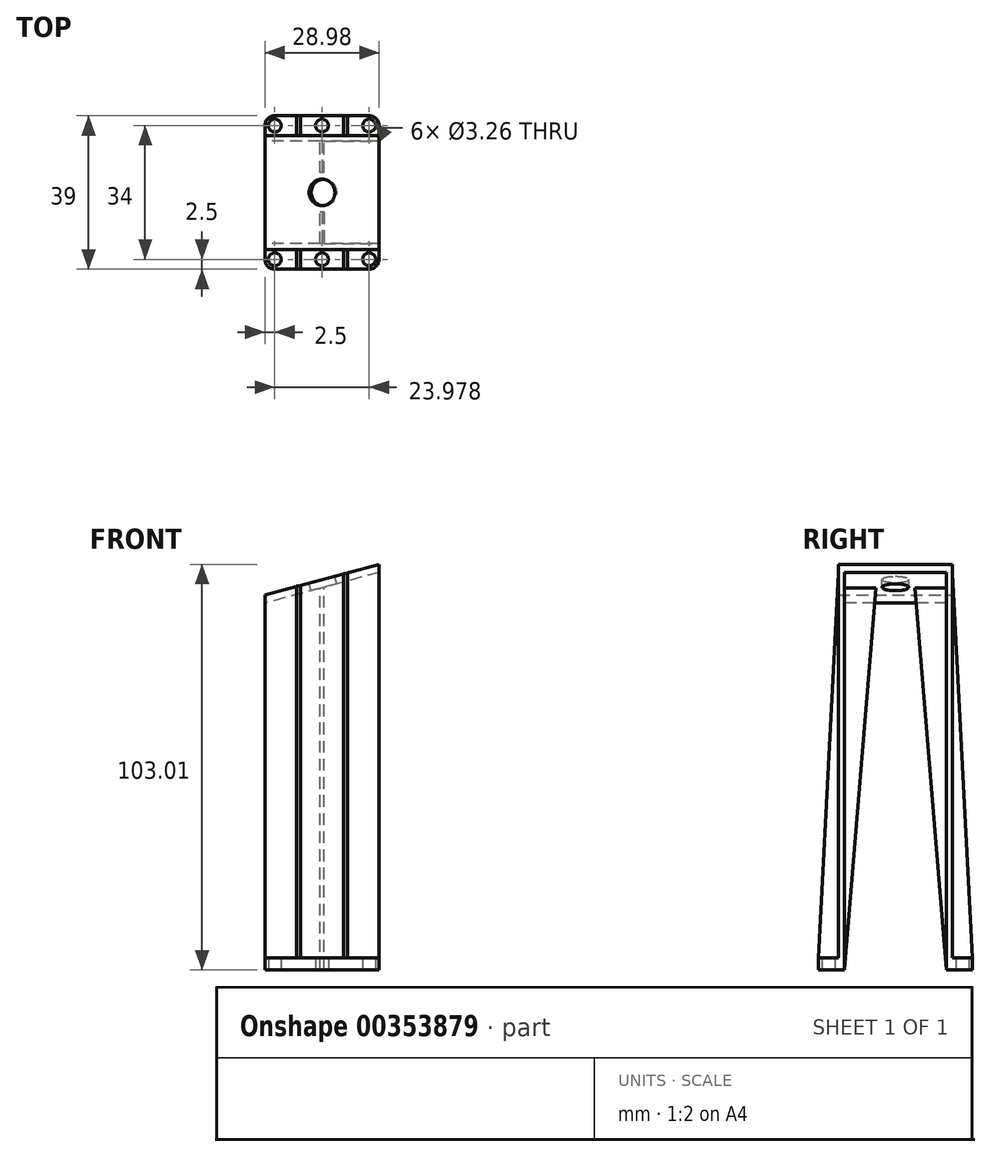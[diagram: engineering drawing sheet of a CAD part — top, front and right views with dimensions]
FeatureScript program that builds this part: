
annotation { "Feature Type Name" : "Feature", "Feature Type Description" : "" }
export const myFeature = defineFeature(function(context is Context, id is Id, definition is map)
    precondition{}
    {
        {
            var Q0;
            Q0=qCreatedBy(makeId("Front.planeOp"),FACE);
            var sketch = newSketch(context, id + "F0", { "sketchPlane" : qUnion([Q0])});
            skLineSegment(sketch, "E0", {"start": v(0, 0) * mm, "end": v(28.98, 7.76) * mm});
            skLineSegment(sketch, "E1", {"start": v(28.98, 7.76) * mm, "end": v(28.98, 0) * mm});
            skLineSegment(sketch, "E2", {"start": v(28.98, 0) * mm, "end": v(0, 0) * mm});
            skLineSegment(sketch, "E3.top", {"start": v(28.98, -95.25) * mm, "end": v(0, -95.25) * mm});
            skLineSegment(sketch, "E3.left", {"start": v(28.98, 0) * mm, "end": v(28.98, -95.25) * mm});
            skLineSegment(sketch, "E3.right", {"start": v(0, 0) * mm, "end": v(0, -95.25) * mm});
            skSolve(sketch);
        }
        {
            var Q0;
            Q0=makeQuery(id+"F0.imprint","IMPRINT",FACE,{"disambiguationData":[TD([[makeQuery(id+"F0.imprint","IMPRINT",EDGE,{"derivedFrom":sQuery(id+"F0.wireOp",EDGE,"E0")}),-1.0]])]});
            var Q1;
            Q1=sQuery(id+"F0.wireOp",EDGE,"E0");
            var Q2;
            Q2=sQuery(id+"F0.wireOp",EDGE,"E1");
            var Q3;
            Q3=sQuery(id+"F0.wireOp",EDGE,"E3.left");
            var Q4;
            Q4=sQuery(id+"F0.wireOp",EDGE,"E3.top");
            var Q5;
            Q5=sQuery(id+"F0.wireOp",EDGE,"E3.right");
            extrude(context, id + "F1", {"entities" : qUnion([Q0]), "surfaceEntities" : qUnion([Q1, Q2, Q3, Q4, Q5]), "depth" : 29 * mm});
        }
        {
            var Q0;
            Q0 = qSketchRegion(id + "F0", true);
            extrude(context, id + "F2", {"entities" : qUnion([Q0]), "operationType" : NewBodyOperationType.ADD, "depth" : 29 * mm});
        }
        {
            var Q0;
            Q0=makeQuery(id+"F1.opExtrude","SWEPT_FACE",FACE,{"disambiguationData":[OSD([sQuery(id+"F0.wireOp",EDGE,"E0")])]});
            var sketch = newSketch(context, id + "F3", { "sketchPlane" : qUnion([Q0])});
            skPoint(sketch, "E4", {"position": v(0, -14.5) * mm});
            skPoint(sketch, "E5", {"position": v(15, 0) * mm});
            skLineSegment(sketch, "E6", {"start": v(0, -14.5) * mm, "end": v(30, -14.5) * mm});
            skLineSegment(sketch, "E7", {"start": v(15, 0) * mm, "end": v(15, -29) * mm});
            skPoint(sketch, "E8", {"position": v(15, -20.5) * mm});
            skPoint(sketch, "E9", {"position": v(26, -14.5) * mm});
            skLineSegment(sketch, "E10.bottom", {"start": v(15, -20.5) * mm, "end": v(26, -20.5) * mm});
            skLineSegment(sketch, "E10.top", {"start": v(15, -14.5) * mm, "end": v(26, -14.5) * mm});
            skLineSegment(sketch, "E10.left", {"start": v(15, -20.5) * mm, "end": v(15, -14.5) * mm});
            skLineSegment(sketch, "E10.right", {"start": v(26, -20.5) * mm, "end": v(26, -14.5) * mm});
            skPoint(sketch, "E11", {"position": v(26, -20.5) * mm});
            skCircle(sketch, "E12", {"center": v(26, -20.5) * mm, "radius": 1.2 * mm});
            skCircle(sketch, "E13.MirrorC", {"center": v(4, -20.5) * mm, "radius": 1.2 * mm});
            skCircle(sketch, "E14.MirrorC", {"center": v(4, -8.5) * mm, "radius": 1.2 * mm});
            skCircle(sketch, "E15.MirrorC", {"center": v(26, -8.5) * mm, "radius": 1.2 * mm});
            skSolve(sketch);
        }
        {
            var Q0;
            Q0=makeQuery(id+"F2.opExtrude","SWEPT_FACE",FACE,{"disambiguationData":[OSD([sQuery(id+"F0.wireOp",EDGE,"E3.top")])]});
            var sketch = newSketch(context, id + "F4", { "sketchPlane" : qUnion([Q0])});
            skPoint(sketch, "E16", {"position": v(2.5, 31.5) * mm});
            skLineSegment(sketch, "E17", {"start": v(14.49, 29) * mm, "end": v(14.49, 0) * mm});
            skPoint(sketch, "E18.MirrorP", {"position": v(26.48, 31.5) * mm});
            skPoint(sketch, "E19", {"position": v(14.49, 31.5) * mm});
            skLineSegment(sketch, "E20.bottom", {"start": v(28.98, 29) * mm, "end": v(0, 29) * mm});
            skLineSegment(sketch, "E20.top", {"start": v(28.98, 34) * mm, "end": v(0, 34) * mm});
            skLineSegment(sketch, "E20.left", {"start": v(28.98, 29) * mm, "end": v(28.98, 34) * mm});
            skLineSegment(sketch, "E20.right", {"start": v(0, 29) * mm, "end": v(0, 34) * mm});
            skLineSegment(sketch, "E21", {"start": v(0, 14.5) * mm, "end": v(28.98, 14.5) * mm});
            skLineSegment(sketch, "E22.MirrorCS", {"start": v(28.98, 0) * mm, "end": v(0, 0) * mm});
            skLineSegment(sketch, "E23.MirrorCS", {"start": v(0, 0) * mm, "end": v(0, -5) * mm});
            skLineSegment(sketch, "E24.MirrorCS", {"start": v(28.98, -5) * mm, "end": v(0, -5) * mm});
            skLineSegment(sketch, "E25.MirrorCS", {"start": v(28.98, 0) * mm, "end": v(28.98, -5) * mm});
            skPoint(sketch, "E26.MirrorP", {"position": v(26.48, -2.5) * mm});
            skPoint(sketch, "E27.MirrorP", {"position": v(14.49, -2.5) * mm});
            skPoint(sketch, "E28.MirrorP", {"position": v(2.5, -2.5) * mm});
            skSolve(sketch);
        }
        {
            var Q0;
            Q0=makeQuery(id+"F4.imprint","IMPRINT",FACE,{"disambiguationData":[TD([[makeQuery(id+"F4.imprint","IMPRINT",EDGE,{"derivedFrom":sQuery(id+"F4.wireOp",EDGE,"E20.top")}),1.0]])]});
            var Q1;
            {var subQ4=sQuery(id+"F4.wireOp",EDGE,"c207b0aa-8032-4c64-916d-486b236da78c0.MirrorCS");Q1=makeQuery(id+"F4.imprint","IMPRINT",FACE,{"disambiguationData":[TD([[makeQuery(id+"F4.imprint","IMPRINT",EDGE,{"derivedFrom":subQ4}),1.0]])]});}
            var Q2;
            {var subQ0=sQuery(id+"F4.wireOp",EDGE,"E23.MirrorCS");Q2=makeQuery(id+"F4.imprint","IMPRINT",FACE,{"disambiguationData":[TD([[makeQuery(id+"F4.imprint","IMPRINT",EDGE,{"derivedFrom":subQ0}),1.0]])]});}
            extrude(context, id + "F5", {"entities" : qUnion([Q0, Q1, Q2]), "operationType" : NewBodyOperationType.ADD, "oppositeDirection" : true, "depth" : 3 * mm});
        }
        {
            var Q0;
            Q0=makeQuery(id+"F5.opExtrude","SWEPT_EDGE",EDGE,{"disambiguationData":[OSD([sQuery(id+"F4.wireOp",EDGE,"E20.top"),sQuery(id+"F4.wireOp",EDGE,"E20.left")])]});
            var Q1;
            Q1=makeQuery(id+"F5.opExtrude","SWEPT_EDGE",EDGE,{"disambiguationData":[OSD([sQuery(id+"F4.wireOp",EDGE,"E20.top"),sQuery(id+"F4.wireOp",EDGE,"E20.right")])]});
            var Q2;
            Q2=makeQuery(id+"F5.opExtrude","SWEPT_EDGE",EDGE,{"disambiguationData":[OSD([sQuery(id+"F4.wireOp",EDGE,"fb5fafe6-6dba-495f-bc75-69146ea7bf050.MirrorCS"),sQuery(id+"F4.wireOp",EDGE,"04278182-d480-4ec0-bce9-3d76de338e120.MirrorCS")])]});
            var Q3;
            Q3=makeQuery(id+"F5.opExtrude","SWEPT_EDGE",EDGE,{"disambiguationData":[OSD([sQuery(id+"F4.wireOp",EDGE,"c207b0aa-8032-4c64-916d-486b236da78c0.MirrorCS"),sQuery(id+"F4.wireOp",EDGE,"fb5fafe6-6dba-495f-bc75-69146ea7bf050.MirrorCS")])]});
            fillet(context, id + "F6", {"entities" : qUnion([Q0, Q1, Q2, Q3]), "radius" : 2.5 * mm, "tangentPropagation" : true, "allowEdgeOverflow" : false});
        }
        {
            var Q0;
            Q0=sQuery(id+"F4.wireOp",VERTEX,"1afc1c53-2bd5-44ff-b609-8fd2801f01ae0.MirrorP");
            var Q1;
            Q1=sQuery(id+"F4.wireOp",VERTEX,"2608caf0-84c1-456a-a7c5-d9c789f694d10.MirrorP");
            var Q2;
            Q2=sQuery(id+"F4.wireOp",VERTEX,"cd476bde-2b93-4753-bf9c-91846a678cbf0.MirrorP");
            var Q3;
            Q3=sQuery(id+"F4.wireOp",VERTEX,"E16");
            var Q4;
            Q4=sQuery(id+"F4.wireOp",VERTEX,"E19");
            var Q5;
            Q5=sQuery(id+"F4.wireOp",VERTEX,"E18.MirrorP");
            var Q6;
            Q6=sQuery(id+"F4.wireOp",VERTEX,"E28.MirrorP");
            var Q7;
            Q7=sQuery(id+"F4.wireOp",VERTEX,"E27.MirrorP");
            var Q8;
            Q8=sQuery(id+"F4.wireOp",VERTEX,"E26.MirrorP");
            var Q9;
            Q9=makeQuery(id+"F1.opExtrude","SWEPT_BODY",BODY,{"disambiguationData":[OSD([sQuery(id+"F0.wireOp",EDGE,"E0"),sQuery(id+"F0.wireOp",EDGE,"E1"),sQuery(id+"F0.wireOp",EDGE,"E2")])]});
            hole(context, id + "F7", {"style" : HoleStyle.SIMPLE, "endStyle" : HoleEndStyle.THROUGH, "holeDiameter" : 3.26 * mm, "isTappedThrough" : true, "tappedDepth" : 12.7 * mm, "tapClearance" : 3, "locations" : qUnion([Q0, Q1, Q2, Q3, Q4, Q5, Q6, Q7, Q8]), "scope" : qUnion([Q9])});
        }
        {
            var Q0;
            Q0=makeQuery(id+"F1.opExtrude","SWEPT_FACE",FACE,{"disambiguationData":[OSD([sQuery(id+"F0.wireOp",EDGE,"E0")])]});
            cPlane(context, id + "F8", {"entities" : qUnion([Q0]), "cplaneType" : CPlaneType.OFFSET, "offset" : 2 * mm, "oppositeDirection" : true, "width" : 152.4 * mm, "height" : 152.4 * mm});
        }
        {
            var Q0;
            Q0=qCreatedBy(id+"F8.planeOp",FACE);
            var sketch = newSketch(context, id + "F9", { "sketchPlane" : qUnion([Q0])});
            skLineSegment(sketch, "E29", {"start": v(-0.54, -29) * mm, "end": v(29.46, -29) * mm});
            skLineSegment(sketch, "E30", {"start": v(-0.54, 0) * mm, "end": v(29.46, 0) * mm});
            skLineSegment(sketch, "E31", {"start": v(29.46, -29) * mm, "end": v(29.46, 0) * mm});
            skLineSegment(sketch, "E32.bottom", {"start": v(29.46, -27.5) * mm, "end": v(-30.54, -27.5) * mm});
            skLineSegment(sketch, "E32.top", {"start": v(29.46, -1.5) * mm, "end": v(-30.54, -1.5) * mm});
            skLineSegment(sketch, "E32.left", {"start": v(29.46, -27.5) * mm, "end": v(29.46, -1.5) * mm});
            skLineSegment(sketch, "E32.right", {"start": v(-30.54, -27.5) * mm, "end": v(-30.54, -1.5) * mm});
            skPoint(sketch, "E32.middle", {"position": v(-0.54, -14.5) * mm});
            skSolve(sketch);
        }
        {
            var Q0;
            Q0=makeQuery(id+"F5.opExtrude","SWEPT_EDGE",EDGE,{"disambiguationData":[OSD([sQuery(id+"F4.wireOp",EDGE,"E24.MirrorCS"),sQuery(id+"F4.wireOp",EDGE,"E25.MirrorCS")])]});
            var Q1;
            Q1=makeQuery(id+"F5.opExtrude","SWEPT_EDGE",EDGE,{"disambiguationData":[OSD([sQuery(id+"F4.wireOp",EDGE,"E23.MirrorCS"),sQuery(id+"F4.wireOp",EDGE,"E24.MirrorCS")])]});
            fillet(context, id + "F10", {"entities" : qUnion([Q0, Q1]), "radius" : 2.5 * mm, "tangentPropagation" : true, "allowEdgeOverflow" : false});
        }
        {
            var Q0;
            Q0=makeQuery(id+"F9.imprint","IMPRINT",FACE,{"disambiguationData":[TD([[makeQuery(id+"F9.imprint","IMPRINT",EDGE,{"derivedFrom":sQuery(id+"F9.wireOp",EDGE,"E32.bottom")}),-1.0]])]});
            var Q1;
            Q1=sQuery(id+"F9.wireOp",EDGE,"E32.bottom");
            var Q2;
            Q2=sQuery(id+"F9.wireOp",EDGE,"E32.right");
            var Q3;
            Q3=sQuery(id+"F9.wireOp",EDGE,"E32.top");
            var Q4;
            Q4=sQuery(id+"F9.wireOp",EDGE,"E32.left");
            extrude(context, id + "F11", {"entities" : qUnion([Q0]), "operationType" : NewBodyOperationType.REMOVE, "surfaceEntities" : qUnion([Q1, Q2, Q3, Q4]), "endBound" : BoundingType.THROUGH_ALL, "oppositeDirection" : true, "depth" : 25 * mm});
        }
        {
            var Q0;
            Q0=makeQuery(id+"F5.opExtrude","CAP_FACE",FACE,{"disambiguationData":[OSD([sQuery(id+"F4.wireOp",EDGE,"E20.bottom"),sQuery(id+"F4.wireOp",EDGE,"E20.top"),sQuery(id+"F4.wireOp",EDGE,"E20.left"),sQuery(id+"F4.wireOp",EDGE,"E20.right")])],"isStart":false});
            var sketch = newSketch(context, id + "F12", { "sketchPlane" : qUnion([Q0])});
            skLineSegment(sketch, "E33", {"start": v(2.5, -31.5) * mm, "end": v(14.49, -31.5) * mm});
            skLineSegment(sketch, "E34", {"start": v(26.48, -31.5) * mm, "end": v(14.49, -31.5) * mm});
            skPoint(sketch, "E35", {"position": v(8.5, -31.5) * mm});
            skPoint(sketch, "E36", {"position": v(20.48, -31.5) * mm});
            skSolve(sketch);
        }
        {
            var Q0;
            Q0=sQuery(id+"F12.wireOp",EDGE,"E34");
            cPoint(context, id + "F13", {"entities" : qUnion([Q0]), "parameter" : 0.5});
        }
        {
            var Q0;
            {var subQ0=sQuery(id+"F0.wireOp",EDGE,"E1");Q0=makeQuery(id+"F5.boolean.opBoolean","MERGE",FACE,{"derivedFrom":[makeQuery(id+"F2.boolean.opBoolean","MERGE",FACE,{"derivedFrom":[makeQuery(id+"F1.opExtrude","SWEPT_FACE",FACE,{"disambiguationData":[OSD([subQ0])]}),makeQuery(id+"F2.opExtrude","SWEPT_FACE",FACE,{"disambiguationData":[OSD([subQ0,sQuery(id+"F0.wireOp",EDGE,"E3.left")])]})]}),makeQuery(id+"F5.opExtrude","SWEPT_FACE",FACE,{"disambiguationData":[OSD([sQuery(id+"F4.wireOp",EDGE,"E20.left")])]}),makeQuery(id+"F5.opExtrude","SWEPT_FACE",FACE,{"disambiguationData":[OSD([sQuery(id+"F4.wireOp",EDGE,"E25.MirrorCS")])]})]});}
            var Q1;
            Q1 = qCreatedBy(id + "F13" ,VERTEX);
            cPlane(context, id + "F14", {"entities" : qUnion([Q0, Q1]), "cplaneType" : CPlaneType.PLANE_POINT, "offset" : 25 * mm, "width" : 150 * mm, "height" : 150 * mm});
        }
        {
            var Q0;
            Q0=qCreatedBy(id+"F14.planeOp",FACE);
            var sketch = newSketch(context, id + "F15", { "sketchPlane" : qUnion([Q0])});
            skLineSegment(sketch, "E37", {"start": v(-29, 5.49) * mm, "end": v(-29, -92.25) * mm});
            skLineSegment(sketch, "E38", {"start": v(-29, -92.25) * mm, "end": v(-34, -92.25) * mm});
            skLineSegment(sketch, "E39", {"start": v(-29, 5.49) * mm, "end": v(-34, -92.25) * mm});
            skLineSegment(sketch, "E40", {"start": v(0, 5.49) * mm, "end": v(0, -92.25) * mm});
            skLineSegment(sketch, "E41", {"start": v(0, -92.25) * mm, "end": v(5, -92.25) * mm});
            skLineSegment(sketch, "E42", {"start": v(0, 5.49) * mm, "end": v(5, -92.25) * mm});
            skSolve(sketch);
        }
        {
            var Q0;
            Q0=makeQuery(id+"F15.imprint","IMPRINT",FACE,{"disambiguationData":[TD([[makeQuery(id+"F15.imprint","IMPRINT",EDGE,{"derivedFrom":sQuery(id+"F15.wireOp",EDGE,"E37")}),-1.0]])]});
            var Q1;
            Q1=makeQuery(id+"F15.imprint","IMPRINT",FACE,{"disambiguationData":[TD([[makeQuery(id+"F15.imprint","IMPRINT",EDGE,{"derivedFrom":sQuery(id+"F15.wireOp",EDGE,"E40")}),1.0]])]});
            extrude(context, id + "F16", {"entities" : qUnion([Q0, Q1]), "operationType" : NewBodyOperationType.ADD, "endBound" : BoundingType.SYMMETRIC, "depth" : 1 * mm});
        }
        {
            var Q0;
            {var subQ0=sQuery(id+"F0.wireOp",EDGE,"E1");Q0=makeQuery(id+"F5.boolean.opBoolean","MERGE",FACE,{"derivedFrom":[makeQuery(id+"F2.boolean.opBoolean","MERGE",FACE,{"derivedFrom":[makeQuery(id+"F1.opExtrude","SWEPT_FACE",FACE,{"disambiguationData":[OSD([subQ0])]}),makeQuery(id+"F2.opExtrude","SWEPT_FACE",FACE,{"disambiguationData":[OSD([subQ0,sQuery(id+"F0.wireOp",EDGE,"E3.left")])]})]}),makeQuery(id+"F5.opExtrude","SWEPT_FACE",FACE,{"disambiguationData":[OSD([sQuery(id+"F4.wireOp",EDGE,"E20.left")])]}),makeQuery(id+"F5.opExtrude","SWEPT_FACE",FACE,{"disambiguationData":[OSD([sQuery(id+"F4.wireOp",EDGE,"E25.MirrorCS")])]})]});}
            var Q1;
            Q1=sQuery(id+"F12.wireOp",VERTEX,"E35");
            cPlane(context, id + "F17", {"entities" : qUnion([Q0, Q1]), "cplaneType" : CPlaneType.PLANE_POINT, "offset" : 25 * mm, "width" : 150 * mm, "height" : 150 * mm});
        }
        {
            var Q0;
            Q0=qCreatedBy(id+"F17.planeOp",FACE);
            var sketch = newSketch(context, id + "F18", { "sketchPlane" : qUnion([Q0])});
            skLineSegment(sketch, "E43", {"start": v(-29, -92.25) * mm, "end": v(-34, -92.25) * mm});
            skLineSegment(sketch, "E44", {"start": v(-29, 2.28) * mm, "end": v(-29, -92.25) * mm});
            skLineSegment(sketch, "E45", {"start": v(-29, 2.28) * mm, "end": v(-34, -92.25) * mm});
            skLineSegment(sketch, "E46", {"start": v(0, 2.28) * mm, "end": v(0, -92.25) * mm});
            skLineSegment(sketch, "E47", {"start": v(0, -92.25) * mm, "end": v(5, -92.25) * mm});
            skLineSegment(sketch, "E48", {"start": v(0, 2.28) * mm, "end": v(5, -92.25) * mm});
            skSolve(sketch);
        }
        {
            var Q0;
            Q0=makeQuery(id+"F18.imprint","IMPRINT",FACE,{"disambiguationData":[TD([[makeQuery(id+"F18.imprint","IMPRINT",EDGE,{"derivedFrom":sQuery(id+"F18.wireOp",EDGE,"E46")}),1.0]])]});
            var Q1;
            Q1=makeQuery(id+"F18.imprint","IMPRINT",FACE,{"disambiguationData":[TD([[makeQuery(id+"F18.imprint","IMPRINT",EDGE,{"derivedFrom":sQuery(id+"F18.wireOp",EDGE,"E43")}),-1.0]])]});
            extrude(context, id + "F19", {"entities" : qUnion([Q0, Q1]), "operationType" : NewBodyOperationType.ADD, "endBound" : BoundingType.SYMMETRIC, "depth" : 1 * mm});
        }
        {
            var Q0;
            Q0=qCreatedBy(id+"F14.planeOp",FACE);
            var Q1;
            Q1=sQuery(id+"F12.wireOp",VERTEX,"E34.end");
            cPlane(context, id + "F20", {"entities" : qUnion([Q0, Q1]), "cplaneType" : CPlaneType.PLANE_POINT, "offset" : 25 * mm, "width" : 150 * mm, "height" : 150 * mm});
        }
        {
            var Q0;
            Q0=qCreatedBy(id+"F20.planeOp",FACE);
            var sketch = newSketch(context, id + "F21", { "sketchPlane" : qUnion([Q0])});
            skLineSegment(sketch, "E49", {"start": v(-27.5, -95.25) * mm, "end": v(-27.5, 1.81) * mm});
            skLineSegment(sketch, "E50", {"start": v(-1.5, 1.81) * mm, "end": v(-27.5, 1.81) * mm});
            skLineSegment(sketch, "E51", {"start": v(-1.5, -95.25) * mm, "end": v(-1.5, 1.81) * mm});
            skLineSegment(sketch, "E52", {"start": v(-14.5, 1.81) * mm, "end": v(-14.5, -95.96) * mm});
            skLineSegment(sketch, "E53", {"start": v(-19.5, 1.81) * mm, "end": v(-27.5, -95.25) * mm});
            skLineSegment(sketch, "E54.MirrorCS", {"start": v(-9.5, 1.81) * mm, "end": v(-1.5, -95.25) * mm});
            skSolve(sketch);
        }
        {
            var Q0;
            {var subQ0=sQuery(id+"F21.wireOp",EDGE,"E49");Q0=makeQuery(id+"F21.imprint","IMPRINT",FACE,{"disambiguationData":[TD([[makeQuery(id+"F21.imprint","IMPRINT",EDGE,{"derivedFrom":subQ0}),-1.0]])]});}
            var Q1;
            {var subQ0=sQuery(id+"F21.wireOp",EDGE,"E51");Q1=makeQuery(id+"F21.imprint","IMPRINT",FACE,{"disambiguationData":[TD([[makeQuery(id+"F21.imprint","IMPRINT",EDGE,{"derivedFrom":subQ0}),1.0]])]});}
            extrude(context, id + "F22", {"entities" : qUnion([Q0, Q1]), "operationType" : NewBodyOperationType.ADD, "endBound" : BoundingType.SYMMETRIC, "depth" : 1 * mm});
        }
        {
            var Q0;
            Q0=sQuery(id+"F3.wireOp",VERTEX,"E10.left.end");
            var Q1;
            Q1=makeQuery(id+"F1.opExtrude","SWEPT_BODY",BODY,{"disambiguationData":[OSD([sQuery(id+"F0.wireOp",EDGE,"E0"),sQuery(id+"F0.wireOp",EDGE,"E1"),sQuery(id+"F0.wireOp",EDGE,"E2")])]});
            hole(context, id + "F23", {"style" : HoleStyle.SIMPLE, "endStyle" : HoleEndStyle.THROUGH, "standardTappedOrClearance" : lookupTablePath({ "standard" : "ANSI", "fit" : "Normal (ASME)", "size" : "1/4", "type" : "Clearance" }), "standardBlindInLast" : lookupTablePath({ "fit" : "Free", "standard" : "ANSI", "size" : "1/4", "type" : "Clearance" }), "holeDiameter" : 6.76 * mm, "isTappedThrough" : true, "tappedDepth" : 12.7 * mm, "tapClearance" : 3, "locations" : qUnion([Q0]), "scope" : qUnion([Q1])});
        }
    });
